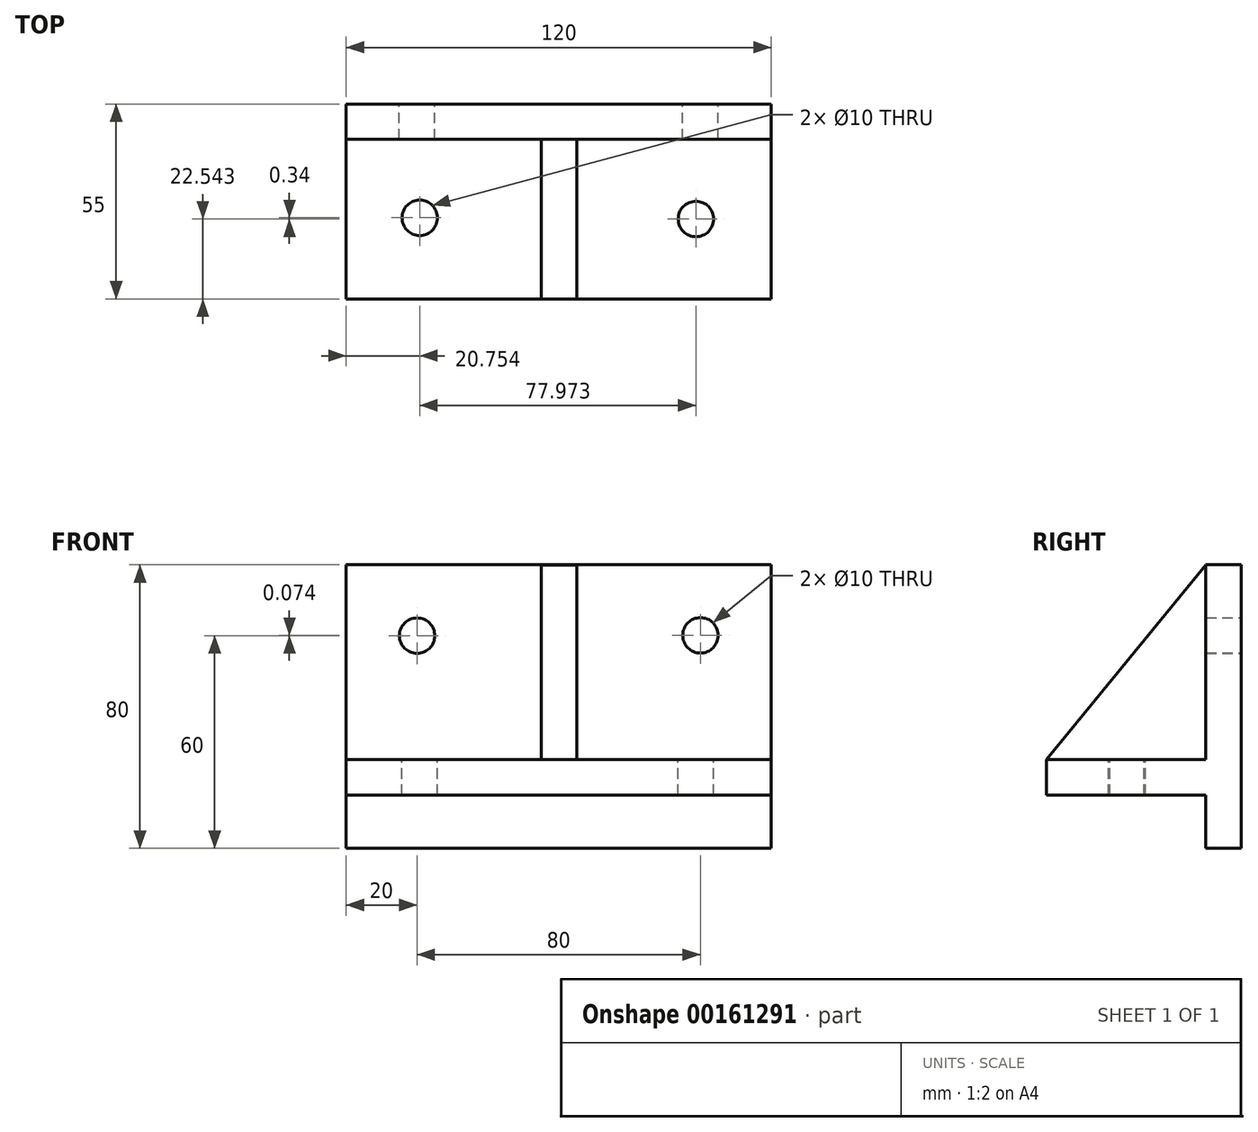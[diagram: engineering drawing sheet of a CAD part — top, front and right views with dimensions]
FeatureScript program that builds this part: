
annotation { "Feature Type Name" : "Feature", "Feature Type Description" : "" }
export const myFeature = defineFeature(function(context is Context, id is Id, definition is map)
    precondition{}
    {
        {
            var Q0;
            Q0=qCreatedBy(makeId("Front.planeOp"),FACE);
            var sketch = newSketch(context, id + "F0", { "sketchPlane" : qUnion([Q0])});
            skLineSegment(sketch, "E0.bottom", {"start": v(-60, 40) * mm, "end": v(60, 40) * mm});
            skLineSegment(sketch, "E0.top", {"start": v(-60, -40) * mm, "end": v(60, -40) * mm});
            skLineSegment(sketch, "E0.left", {"start": v(-60, 40) * mm, "end": v(-60, -40) * mm});
            skLineSegment(sketch, "E0.right", {"start": v(60, 40) * mm, "end": v(60, -40) * mm});
            skPoint(sketch, "E0.middle", {"position": v(0, 0) * mm});
            skCircle(sketch, "E1", {"center": v(-40, 20) * mm, "radius": 5 * mm});
            skCircle(sketch, "E2", {"center": v(40, 20.07) * mm, "radius": 5 * mm});
            skSolve(sketch);
        }
        {
            var Q0;
            Q0 = qSketchRegion(id + "F0", true);
            var Q1;
            Q1 = qSketchRegion(id + "FfXocxBMdQYhgHu_1", true);
            extrude(context, id + "F1", {"entities" : qUnion([Q0, Q1]), "depth" : 10 * mm});
        }
        {
            var Q0;
            Q0=makeQuery(id+"F1.opExtrude","CAP_FACE",FACE,{"disambiguationData":[OSD([sQuery(id+"F0.wireOp",EDGE,"E0.bottom"),sQuery(id+"F0.wireOp",EDGE,"E0.top"),sQuery(id+"F0.wireOp",EDGE,"E0.left"),sQuery(id+"F0.wireOp",EDGE,"E0.right"),sQuery(id+"F0.wireOp",EDGE,"E1"),sQuery(id+"F0.wireOp",EDGE,"E2")])],"isStart":false});
            var sketch = newSketch(context, id + "F2", { "sketchPlane" : qUnion([Q0])});
            skLineSegment(sketch, "E3.bottom", {"start": v(-60, -25) * mm, "end": v(60, -25) * mm});
            skLineSegment(sketch, "E3.top", {"start": v(-60, -15) * mm, "end": v(60, -15) * mm});
            skLineSegment(sketch, "E3.left", {"start": v(-60, -25) * mm, "end": v(-60, -15) * mm});
            skLineSegment(sketch, "E3.right", {"start": v(60, -25) * mm, "end": v(60, -15) * mm});
            skSolve(sketch);
        }
        {
            var Q0;
            Q0 = qSketchRegion(id + "F2", true);
            var Q1;
            Q1 = qSketchRegion(id + "FE8ySRNIR3oGcJs_1", true);
            extrude(context, id + "F3", {"entities" : qUnion([Q0, Q1]), "operationType" : NewBodyOperationType.ADD, "depth" : 45 * mm});
        }
        {
            var Q0;
            {var subQ1=sQuery(id+"F2.wireOp",EDGE,"E3.top");var subQ3=sQuery(id+"F0.wireOp",EDGE,"E0.left");Q0=makeQuery(id+"FON1hWuiETzKv8f_1.boolean.opBoolean","SPLIT",FACE,{"disambiguationData":[TD([makeQuery(id+"F1.opExtrude","SWEPT_FACE",FACE,{"disambiguationData":[OSD([subQ3])]})])],"derivedFrom":makeQuery(id+"F3.opExtrude","SWEPT_FACE",FACE,{"disambiguationData":[OSD([subQ1])]})});}
            var sketch = newSketch(context, id + "F4", { "sketchPlane" : qUnion([Q0])});
            skCircle(sketch, "E4", {"center": v(-39.25, -32.12) * mm, "radius": 5 * mm});
            skCircle(sketch, "E5", {"center": v(38.73, -32.46) * mm, "radius": 5 * mm});
            skSolve(sketch);
        }
        {
            var Q0;
            Q0 = qSketchRegion(id + "F4", true);
            extrude(context, id + "F5", {"entities" : qUnion([Q0]), "operationType" : NewBodyOperationType.REMOVE, "oppositeDirection" : true, "depth" : 25 * mm});
        }
        {
            var Q0;
            {var subQ0=sQuery(id+"F0.wireOp",EDGE,"E1");var subQ1=sQuery(id+"F0.wireOp",EDGE,"E0.right");var subQ2=sQuery(id+"F0.wireOp",EDGE,"E0.left");var subQ3=sQuery(id+"F0.wireOp",EDGE,"E0.bottom");var subQ4=sQuery(id+"F0.wireOp",EDGE,"E2");Q0=makeQuery(id+"F3.boolean.opBoolean","SPLIT",FACE,{"disambiguationData":[TD([makeQuery(id+"F1.opExtrude","SWEPT_FACE",FACE,{"disambiguationData":[OSD([subQ3])]})])],"derivedFrom":makeQuery(id+"F1.opExtrude","CAP_FACE",FACE,{"disambiguationData":[OSD([subQ3,sQuery(id+"F0.wireOp",EDGE,"E0.top"),subQ2,subQ1,subQ0,subQ4])],"isStart":false})});}
            var sketch = newSketch(context, id + "F6", { "sketchPlane" : qUnion([Q0])});
            skLineSegment(sketch, "E6", {"start": v(-4.95, 39.96) * mm, "end": v(5.05, 39.96) * mm});
            skLineSegment(sketch, "E7.top", {"start": v(-4.95, -15) * mm, "end": v(5.05, -15) * mm});
            skLineSegment(sketch, "E7.left", {"start": v(-4.95, 39.96) * mm, "end": v(-4.95, -15) * mm});
            skLineSegment(sketch, "E7.right", {"start": v(5.05, 39.96) * mm, "end": v(5.05, -15) * mm});
            skSolve(sketch);
        }
        {
            var Q0;
            Q0 = qSketchRegion(id + "F6", true);
            extrude(context, id + "F7", {"entities" : qUnion([Q0]), "operationType" : NewBodyOperationType.ADD, "depth" : 45 * mm});
        }
        {
            var Q0;
            Q0=makeQuery(id+"F7.opExtrude","SWEPT_FACE",FACE,{"disambiguationData":[OSD([sQuery(id+"F6.wireOp",EDGE,"E7.left")])]});
            var sketch = newSketch(context, id + "F8", { "sketchPlane" : qUnion([Q0])});
            skLineSegment(sketch, "E8", {"start": v(10, 39.96) * mm, "end": v(55, -15) * mm});
            skLineSegment(sketch, "E9", {"start": v(55, -15) * mm, "end": v(55, 39.96) * mm});
            skLineSegment(sketch, "E10", {"start": v(55, 39.96) * mm, "end": v(10, 39.96) * mm});
            skSolve(sketch);
        }
        {
            var Q0;
            Q0 = qSketchRegion(id + "F8", true);
            extrude(context, id + "F9", {"entities" : qUnion([Q0]), "operationType" : NewBodyOperationType.REMOVE, "oppositeDirection" : true, "depth" : 25 * mm});
        }
    });
